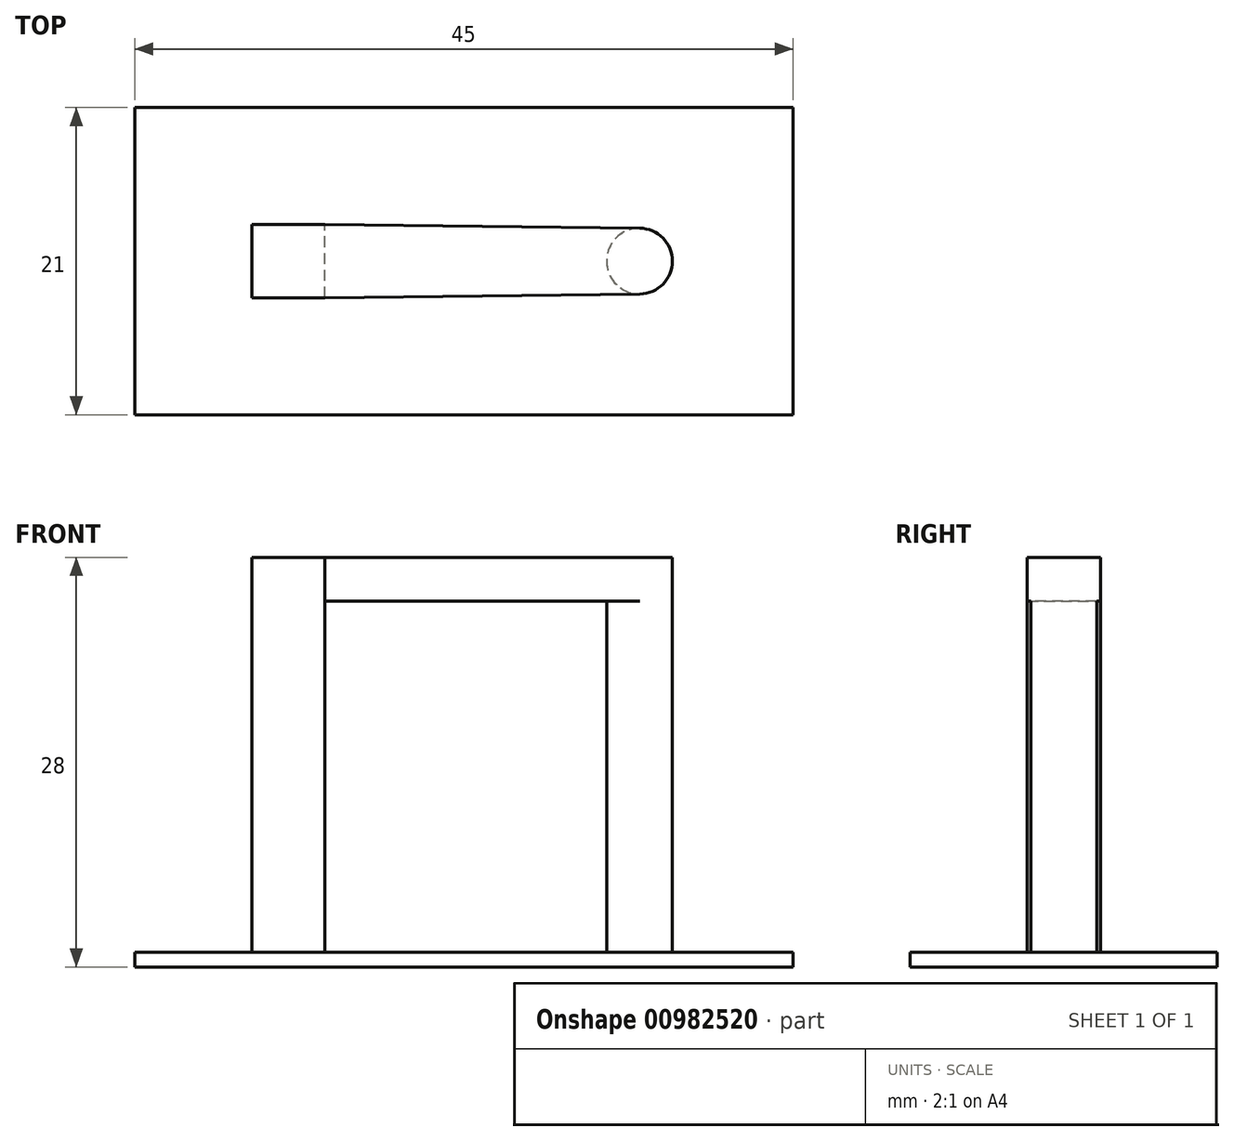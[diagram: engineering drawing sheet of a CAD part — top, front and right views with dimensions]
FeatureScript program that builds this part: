
annotation { "Feature Type Name" : "Feature", "Feature Type Description" : "" }
export const myFeature = defineFeature(function(context is Context, id is Id, definition is map)
    precondition{}
    {
        {
            var Q0;
            Q0=qCreatedBy(makeId("Top.planeOp"),FACE);
            var sketch = newSketch(context, id + "F0", { "sketchPlane" : qUnion([Q0])});
            skLineSegment(sketch, "E0.bottom", {"start": v(-22.5, 10.5) * mm, "end": v(22.5, 10.5) * mm});
            skLineSegment(sketch, "E0.top", {"start": v(-22.5, -10.5) * mm, "end": v(22.5, -10.5) * mm});
            skLineSegment(sketch, "E0.left", {"start": v(-22.5, 10.5) * mm, "end": v(-22.5, -10.5) * mm});
            skLineSegment(sketch, "E0.right", {"start": v(22.5, 10.5) * mm, "end": v(22.5, -10.5) * mm});
            skPoint(sketch, "E0.middle", {"position": v(0, 0) * mm});
            skLineSegment(sketch, "E1.bottom", {"start": v(-9.5, -2.5) * mm, "end": v(-14.5, -2.5) * mm});
            skLineSegment(sketch, "E1.top", {"start": v(-9.5, 2.5) * mm, "end": v(-14.5, 2.5) * mm});
            skLineSegment(sketch, "E1.left", {"start": v(-9.5, -2.5) * mm, "end": v(-9.5, 2.5) * mm});
            skLineSegment(sketch, "E1.right", {"start": v(-14.5, -2.5) * mm, "end": v(-14.5, 2.5) * mm});
            skPoint(sketch, "E1.middle", {"position": v(-12, 0) * mm});
            skCircle(sketch, "E2", {"center": v(12, 0) * mm, "radius": 2.25 * mm});
            skLineSegment(sketch, "E3", {"start": v(-12, 0) * mm, "end": v(0, 0) * mm, "construction": true});
            skLineSegment(sketch, "E4", {"start": v(0, 0) * mm, "end": v(12, 0) * mm, "construction": true});
            skSolve(sketch);
        }
        {
            var Q0;
            Q0 = qSketchRegion(id + "F0", true);
            extrude(context, id + "F1", {"entities" : qUnion([Q0]), "depth" : 1 * mm, "offsetDistance" : 25 * mm});
        }
        {
            var Q0;
            Q0=makeQuery(id+"F0.imprint","IMPRINT",FACE,{"disambiguationData":[TD([[makeQuery(id+"F0.imprint","IMPRINT",EDGE,{"derivedFrom":sQuery(id+"F0.wireOp",EDGE,"E1.bottom")}),-1.0]])]});
            var Q1;
            Q1=makeQuery(id+"F0.imprint","IMPRINT",FACE,{"disambiguationData":[TD([[makeQuery(id+"F0.imprint","IMPRINT",EDGE,{"derivedFrom":sQuery(id+"F0.wireOp",EDGE,"E2")}),1.0]])]});
            extrude(context, id + "F2", {"entities" : qUnion([Q0, Q1]), "operationType" : NewBodyOperationType.ADD, "depth" : 25 * mm, "offsetDistance" : 25 * mm});
        }
        {
            var Q0;
            Q0=makeQuery(id+"F2.opExtrude","CAP_FACE",FACE,{"disambiguationData":[OSD([sQuery(id+"F0.wireOp",EDGE,"E1.bottom"),sQuery(id+"F0.wireOp",EDGE,"E1.top"),sQuery(id+"F0.wireOp",EDGE,"E1.left"),sQuery(id+"F0.wireOp",EDGE,"E1.right")])],"isStart":false});
            var sketch = newSketch(context, id + "F3", { "sketchPlane" : qUnion([Q0])});
            skLineSegment(sketch, "E5", {"start": v(-9.5, 2.5) * mm, "end": v(12.03, 2.25) * mm});
            skLineSegment(sketch, "E6.MirrorCS", {"start": v(-9.5, -2.5) * mm, "end": v(12.03, -2.25) * mm});
            skCircle(sketch, "E7.0", {"center": v(12, 0) * mm, "radius": 2.25 * mm});
            skLineSegment(sketch, "E8.0.0", {"start": v(-9.5, -2.5) * mm, "end": v(-9.5, 2.5) * mm});
            skLineSegment(sketch, "E8.0.1", {"start": v(-9.5, 2.5) * mm, "end": v(-14.5, 2.5) * mm});
            skLineSegment(sketch, "E8.0.2", {"start": v(-14.5, 2.5) * mm, "end": v(-14.5, -2.5) * mm});
            skLineSegment(sketch, "E8.0.3", {"start": v(-14.5, -2.5) * mm, "end": v(-9.5, -2.5) * mm});
            skSolve(sketch);
        }
        {
            var Q0;
            Q0 = qSketchRegion(id + "F3", true);
            extrude(context, id + "F4", {"entities" : qUnion([Q0]), "operationType" : NewBodyOperationType.ADD, "depth" : 3 * mm, "offsetDistance" : 25 * mm});
        }
    });
